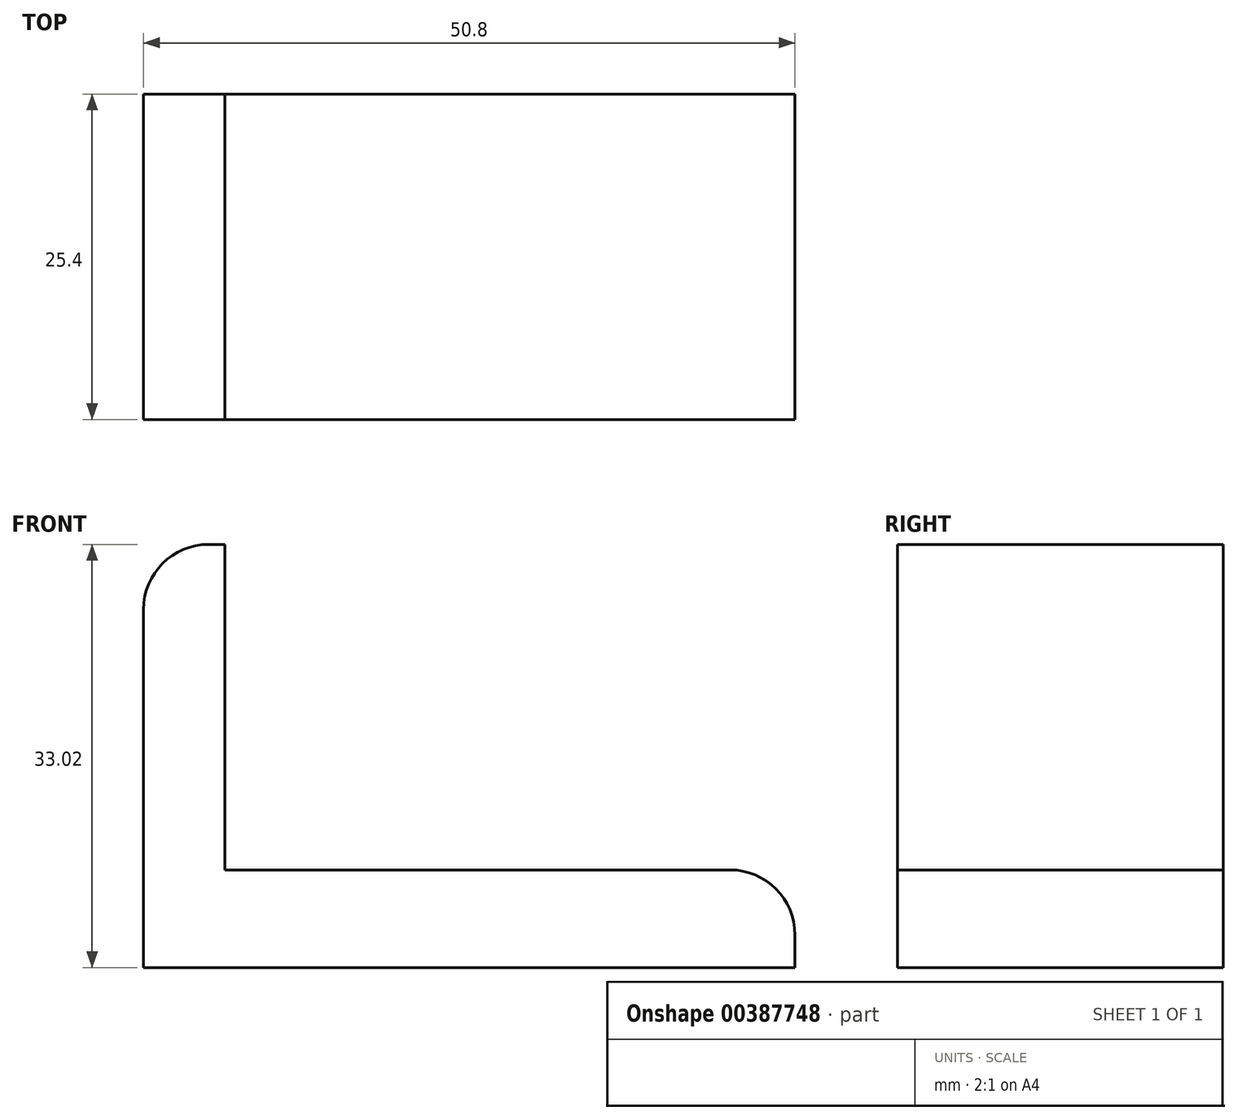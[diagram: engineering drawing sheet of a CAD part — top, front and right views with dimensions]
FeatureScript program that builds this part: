
annotation { "Feature Type Name" : "Feature", "Feature Type Description" : "" }
export const myFeature = defineFeature(function(context is Context, id is Id, definition is map)
    precondition{}
    {
        {
            var Q0;
            Q0=qCreatedBy(makeId("Front.planeOp"),FACE);
            var sketch = newSketch(context, id + "F0", { "sketchPlane" : qUnion([Q0])});
            skLineSegment(sketch, "E0", {"start": v(0, 0) * mm, "end": v(0, 33.02) * mm});
            skLineSegment(sketch, "E1", {"start": v(0, 33.02) * mm, "end": v(6.35, 33.02) * mm});
            skLineSegment(sketch, "E2", {"start": v(6.35, 33.02) * mm, "end": v(6.35, 7.62) * mm});
            skLineSegment(sketch, "E3", {"start": v(6.35, 7.62) * mm, "end": v(50.8, 7.62) * mm});
            skLineSegment(sketch, "E4", {"start": v(50.8, 7.62) * mm, "end": v(50.8, 0) * mm});
            skLineSegment(sketch, "E5", {"start": v(50.8, 0) * mm, "end": v(0, 0) * mm});
            skSolve(sketch);
        }
        {
            var Q0;
            Q0=makeQuery(id+"F0.imprint","IMPRINT",FACE,{"disambiguationData":[TD([[makeQuery(id+"F0.imprint","IMPRINT",EDGE,{"derivedFrom":sQuery(id+"F0.wireOp",EDGE,"E0")}),-1.0]])]});
            extrude(context, id + "F1", {"entities" : qUnion([Q0]), "oppositeDirection" : true, "depth" : 25.4 * mm});
        }
        {
            var Q0;
            Q0=makeQuery(id+"F1.opExtrude","SWEPT_EDGE",EDGE,{"disambiguationData":[OSD([sQuery(id+"F0.wireOp",EDGE,"E0"),sQuery(id+"F0.wireOp",EDGE,"E1")])]});
            var Q1;
            Q1=makeQuery(id+"F1.opExtrude","SWEPT_EDGE",EDGE,{"disambiguationData":[OSD([sQuery(id+"F0.wireOp",EDGE,"E3"),sQuery(id+"F0.wireOp",EDGE,"E4")])]});
            fillet(context, id + "F2", {"entities" : qUnion([Q0, Q1]), "radius" : 5.08 * mm, "tangentPropagation" : true, "allowEdgeOverflow" : false});
        }
    });
